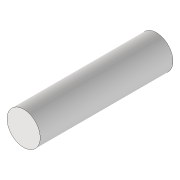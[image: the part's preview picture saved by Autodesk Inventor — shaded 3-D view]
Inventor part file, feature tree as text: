
AUTODESK INVENTOR PART (.ipt)
format: ipt  version: 2020 (Build 240168000, 168)  size: 74,752 bytes
history: native  units: mm
features: sketch x1, extrude x1
ambient origin geometry x8: Origin, YZ Plane, XZ Plane, XY Plane, X Axis, Y Axis, Z Axis, Center Point
bodies: Volumenkörper1 (feature_tree)
feature tree (2):
  sketch  "Skizze1"  dims[d0=0.5mm d2=0.0mm d3=2.0mm]
  extrude  "Extrusion1"  [1 undecoded]
note: 1 required parameter value undecoded (feature->parameter linkage not recoverable at this tier; creation-order binding heuristic only, values carry confidence <= 0.55)
